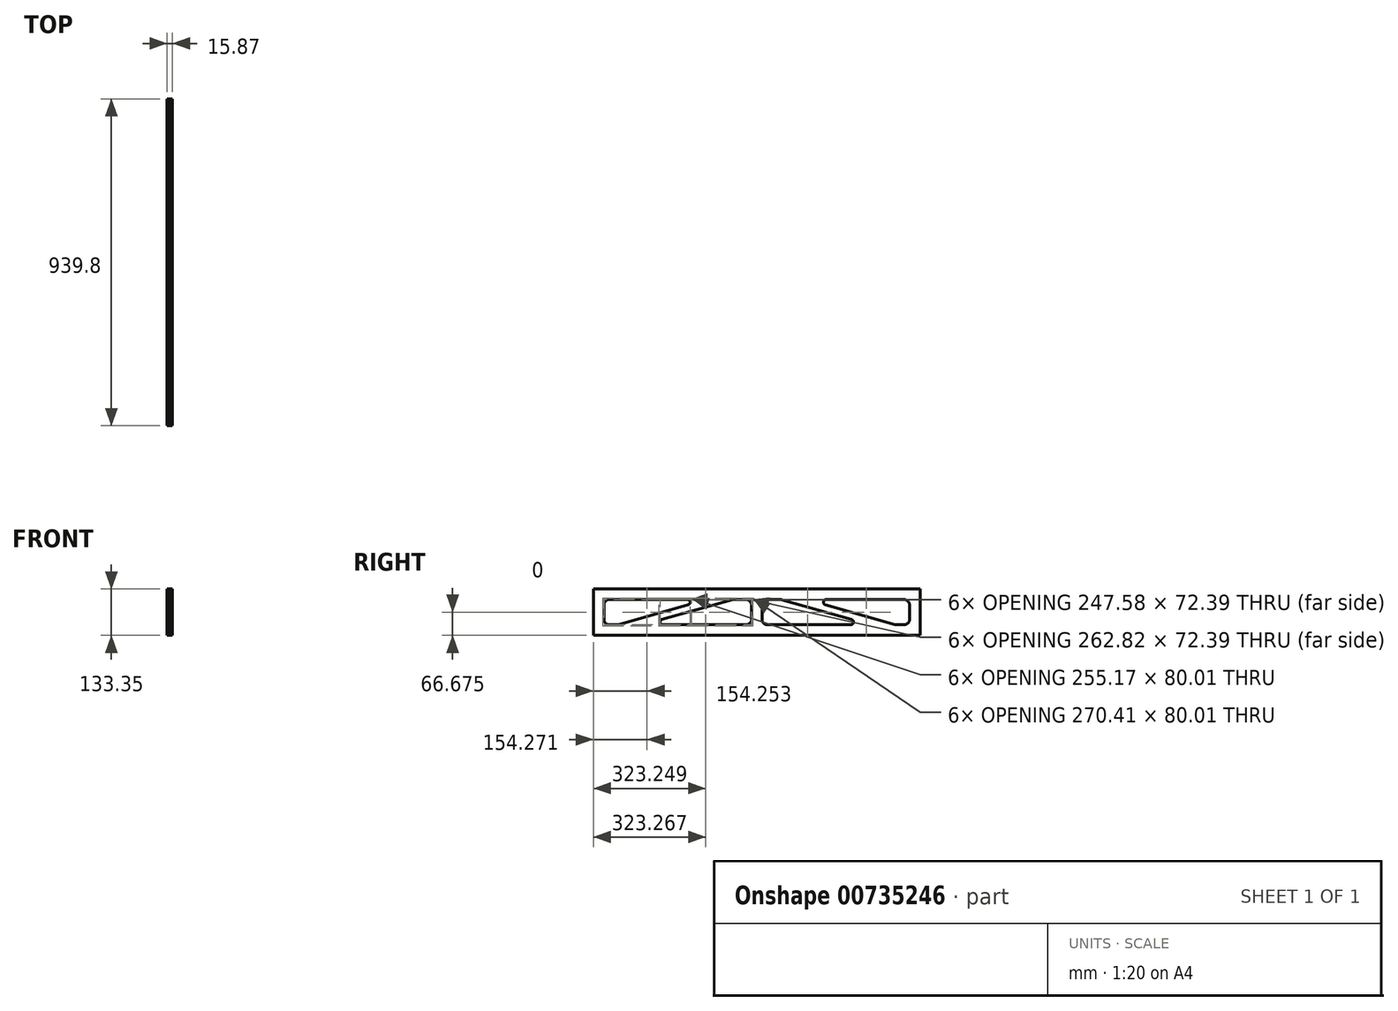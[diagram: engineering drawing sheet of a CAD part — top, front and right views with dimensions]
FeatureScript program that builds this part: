
annotation { "Feature Type Name" : "Feature", "Feature Type Description" : "" }
export const myFeature = defineFeature(function(context is Context, id is Id, definition is map)
    precondition{}
    {
        {
            var Q0;
            Q0=qCreatedBy(makeId("Front.planeOp"),FACE);
            var sketch = newSketch(context, id + "F0", { "sketchPlane" : qUnion([Q0])});
            skLineSegment(sketch, "E0.bottom", {"start": v(247.65, 0) * mm, "end": v(-247.65, 0) * mm});
            skLineSegment(sketch, "E0.top", {"start": v(247.65, 133.35) * mm, "end": v(-247.65, 133.35) * mm});
            skLineSegment(sketch, "E0.left", {"start": v(247.65, 0) * mm, "end": v(247.65, 133.35) * mm});
            skLineSegment(sketch, "E0.right", {"start": v(-247.65, 0) * mm, "end": v(-247.65, 133.35) * mm});
            skPoint(sketch, "E0.middle", {"position": v(0, 66.68) * mm});
            skSolve(sketch);
        }
        {
            var Q0;
            Q0=makeQuery(id+"F0.imprint","IMPRINT",FACE,{"disambiguationData":[TD([[makeQuery(id+"F0.imprint","IMPRINT",EDGE,{"derivedFrom":sQuery(id+"F0.wireOp",EDGE,"E0.bottom")}),-1.0]])]});
            var Q1;
            Q1 = qConstructionFilter(qBodyType(qCreatedBy(id + "F0" ,EDGE), BodyType.WIRE), ConstructionObject.NO);
            extrude(context, id + "F1", {"entities" : qUnion([Q0]), "bodyType" : ToolBodyType.SURFACE, "surfaceEntities" : qUnion([Q1]), "oppositeDirection" : true, "depth" : 939.8 * mm, "offsetDistance" : 25.4 * mm});
        }
        {
            var Q0;
            Q0=makeQuery(id+"F1.opExtrude","SWEPT_FACE",FACE,{"disambiguationData":[OSD([sQuery(id+"F0.wireOp",EDGE,"E0.left")])]});
            var sketch = newSketch(context, id + "F2", { "sketchPlane" : qUnion([Q0])});
            skLineSegment(sketch, "E1.0", {"start": v(0, 0) * mm, "end": v(0, 133.35) * mm});
            skLineSegment(sketch, "E2.0", {"start": v(0, 133.35) * mm, "end": v(-939.8, 133.35) * mm});
            skLineSegment(sketch, "E3.0", {"start": v(0, 0) * mm, "end": v(-939.8, 0) * mm});
            skLineSegment(sketch, "E4.0", {"start": v(-939.8, 133.35) * mm, "end": v(-939.8, 0) * mm});
            skLineSegment(sketch, "E5.0", {"start": v(-30.48, 30.48) * mm, "end": v(-30.48, 102.87) * mm});
            skLineSegment(sketch, "E5.1", {"start": v(-30.48, 30.48) * mm, "end": v(-70.2, 30.48) * mm});
            skLineSegment(sketch, "E5.2", {"start": v(-909.32, 102.87) * mm, "end": v(-909.32, 30.48) * mm});
            skLineSegment(sketch, "E5.3", {"start": v(-30.48, 102.87) * mm, "end": v(-325.28, 102.87) * mm});
            skPoint(sketch, "E6", {"position": v(-469.9, 0) * mm});
            skLineSegment(sketch, "E7", {"start": v(-469.9, 0) * mm, "end": v(-469.9, 133.35) * mm, "construction": true});
            skLineSegment(sketch, "E8", {"start": v(0, 0) * mm, "end": v(-469.9, 133.35) * mm, "construction": true});
            skLineSegment(sketch, "E9", {"start": v(-939.8, 0) * mm, "end": v(-469.9, 133.35) * mm, "construction": true});
            skLineSegment(sketch, "E10", {"start": v(-325.28, 102.87) * mm, "end": v(-70.2, 30.48) * mm});
            skLineSegment(sketch, "E11", {"start": v(-144.62, 30.48) * mm, "end": v(-399.7, 102.87) * mm});
            skLineSegment(sketch, "E12", {"start": v(-454.66, 102.87) * mm, "end": v(-454.66, 30.48) * mm});
            skLineSegment(sketch, "E13", {"start": v(-485.14, 102.87) * mm, "end": v(-485.14, 30.48) * mm});
            skLineSegment(sketch, "E14", {"start": v(-540.1, 102.87) * mm, "end": v(-795.18, 30.48) * mm});
            skLineSegment(sketch, "E15", {"start": v(-614.52, 102.87) * mm, "end": v(-869.6, 30.48) * mm});
            skLineSegment(sketch, "E16.trimOffspring", {"start": v(-399.7, 102.87) * mm, "end": v(-454.66, 102.87) * mm});
            skLineSegment(sketch, "E17.trimOffspring", {"start": v(-144.62, 30.48) * mm, "end": v(-454.66, 30.48) * mm});
            skLineSegment(sketch, "E18.trimOffspring", {"start": v(-485.14, 102.87) * mm, "end": v(-540.1, 102.87) * mm});
            skLineSegment(sketch, "E19.trimOffspring", {"start": v(-485.14, 30.48) * mm, "end": v(-795.18, 30.48) * mm});
            skLineSegment(sketch, "E20.trimOffspring", {"start": v(-614.52, 102.87) * mm, "end": v(-909.32, 102.87) * mm});
            skLineSegment(sketch, "E21.trimOffspring", {"start": v(-869.6, 30.48) * mm, "end": v(-909.32, 30.48) * mm});
            skSolve(sketch);
        }
        {
            var Q0;
            Q0 = qSketchRegion(id + "F2", true);
            extrude(context, id + "F3", {"entities" : qUnion([Q0]), "depth" : 9.52 * mm, "offsetDistance" : 25.4 * mm});
        }
        {
            var Q0;
            Q0=makeQuery(id+"F3.opExtrude","SWEPT_EDGE",EDGE,{"disambiguationData":[OSD([sQuery(id+"F2.wireOp",EDGE,"E11"),sQuery(id+"F2.wireOp",EDGE,"E16.trimOffspring")])]});
            var Q1;
            Q1=makeQuery(id+"F3.opExtrude","SWEPT_EDGE",EDGE,{"disambiguationData":[OSD([sQuery(id+"F2.wireOp",EDGE,"E12"),sQuery(id+"F2.wireOp",EDGE,"E16.trimOffspring")])]});
            var Q2;
            Q2=makeQuery(id+"F3.opExtrude","SWEPT_EDGE",EDGE,{"disambiguationData":[OSD([sQuery(id+"F2.wireOp",EDGE,"E12"),sQuery(id+"F2.wireOp",EDGE,"E17.trimOffspring")])]});
            var Q3;
            Q3=makeQuery(id+"F3.opExtrude","SWEPT_EDGE",EDGE,{"disambiguationData":[OSD([sQuery(id+"F2.wireOp",EDGE,"E5.0"),sQuery(id+"F2.wireOp",EDGE,"E5.1")])]});
            var Q4;
            Q4=makeQuery(id+"F3.opExtrude","SWEPT_EDGE",EDGE,{"disambiguationData":[OSD([sQuery(id+"F2.wireOp",EDGE,"E5.0"),sQuery(id+"F2.wireOp",EDGE,"E5.3")])]});
            var Q5;
            Q5=makeQuery(id+"F3.opExtrude","SWEPT_EDGE",EDGE,{"disambiguationData":[OSD([sQuery(id+"F2.wireOp",EDGE,"E5.1"),sQuery(id+"F2.wireOp",EDGE,"E10")])]});
            var Q6;
            Q6=makeQuery(id+"F3.opExtrude","SWEPT_EDGE",EDGE,{"disambiguationData":[OSD([sQuery(id+"F2.wireOp",EDGE,"E14"),sQuery(id+"F2.wireOp",EDGE,"E18.trimOffspring")])]});
            var Q7;
            Q7=makeQuery(id+"F3.opExtrude","SWEPT_EDGE",EDGE,{"disambiguationData":[OSD([sQuery(id+"F2.wireOp",EDGE,"E13"),sQuery(id+"F2.wireOp",EDGE,"E18.trimOffspring")])]});
            var Q8;
            Q8=makeQuery(id+"F3.opExtrude","SWEPT_EDGE",EDGE,{"disambiguationData":[OSD([sQuery(id+"F2.wireOp",EDGE,"E13"),sQuery(id+"F2.wireOp",EDGE,"E19.trimOffspring")])]});
            var Q9;
            Q9=makeQuery(id+"F3.opExtrude","SWEPT_EDGE",EDGE,{"disambiguationData":[OSD([sQuery(id+"F2.wireOp",EDGE,"E5.2"),sQuery(id+"F2.wireOp",EDGE,"E20.trimOffspring")])]});
            var Q10;
            Q10=makeQuery(id+"F3.opExtrude","SWEPT_EDGE",EDGE,{"disambiguationData":[OSD([sQuery(id+"F2.wireOp",EDGE,"E5.2"),sQuery(id+"F2.wireOp",EDGE,"E21.trimOffspring")])]});
            var Q11;
            Q11=makeQuery(id+"F3.opExtrude","SWEPT_EDGE",EDGE,{"disambiguationData":[OSD([sQuery(id+"F2.wireOp",EDGE,"E15"),sQuery(id+"F2.wireOp",EDGE,"E21.trimOffspring")])]});
            fillet(context, id + "F4", {"entities" : qUnion([Q0, Q1, Q2, Q3, Q4, Q5, Q6, Q7, Q8, Q9, Q10, Q11]), "radius" : 15.24 * mm, "tangentPropagation" : true, "allowEdgeOverflow" : false});
        }
        {
            var Q0;
            Q0=makeQuery(id+"F3.opExtrude","SWEPT_EDGE",EDGE,{"disambiguationData":[OSD([sQuery(id+"F2.wireOp",EDGE,"E11"),sQuery(id+"F2.wireOp",EDGE,"E17.trimOffspring")])]});
            var Q1;
            Q1=makeQuery(id+"F3.opExtrude","SWEPT_EDGE",EDGE,{"disambiguationData":[OSD([sQuery(id+"F2.wireOp",EDGE,"E15"),sQuery(id+"F2.wireOp",EDGE,"E20.trimOffspring")])]});
            var Q2;
            Q2=makeQuery(id+"F3.opExtrude","SWEPT_EDGE",EDGE,{"disambiguationData":[OSD([sQuery(id+"F2.wireOp",EDGE,"E14"),sQuery(id+"F2.wireOp",EDGE,"E19.trimOffspring")])]});
            var Q3;
            Q3=makeQuery(id+"F3.opExtrude","SWEPT_EDGE",EDGE,{"disambiguationData":[OSD([sQuery(id+"F2.wireOp",EDGE,"E5.3"),sQuery(id+"F2.wireOp",EDGE,"E10")])]});
            fillet(context, id + "F5", {"entities" : qUnion([Q0, Q1, Q2, Q3]), "radius" : 7.62 * mm, "tangentPropagation" : true, "allowEdgeOverflow" : false});
        }
        {
            var Q0;
            Q0=makeQuery(id+"F3.opExtrude","CAP_EDGE",EDGE,{"disambiguationData":[OSD([sQuery(id+"F2.wireOp",EDGE,"E5.3")])],"isStart":true});
            var Q1;
            Q1=makeQuery(id+"F3.opExtrude","CAP_EDGE",EDGE,{"disambiguationData":[OSD([sQuery(id+"F2.wireOp",EDGE,"E11")])],"isStart":true});
            var Q2;
            Q2=makeQuery(id+"F3.opExtrude","CAP_EDGE",EDGE,{"disambiguationData":[OSD([sQuery(id+"F2.wireOp",EDGE,"E18.trimOffspring")])],"isStart":true});
            var Q3;
            Q3=makeQuery(id+"F3.opExtrude","CAP_EDGE",EDGE,{"disambiguationData":[OSD([sQuery(id+"F2.wireOp",EDGE,"E20.trimOffspring")])],"isStart":true});
            fillet(context, id + "F6", {"entities" : qUnion([Q0, Q1, Q2, Q3]), "radius" : 3.8 * mm, "tangentPropagation" : true, "allowEdgeOverflow" : false});
        }
        {
            var Q0;
            Q0=makeQuery(id+"F3.opExtrude","CAP_FACE",FACE,{"disambiguationData":[OSD([sQuery(id+"F2.wireOp",EDGE,"E1.0"),sQuery(id+"F2.wireOp",EDGE,"E2.0"),sQuery(id+"F2.wireOp",EDGE,"E3.0"),sQuery(id+"F2.wireOp",EDGE,"E4.0"),sQuery(id+"F2.wireOp",EDGE,"E5.0"),sQuery(id+"F2.wireOp",EDGE,"E5.1"),sQuery(id+"F2.wireOp",EDGE,"E5.2"),sQuery(id+"F2.wireOp",EDGE,"E5.3"),sQuery(id+"F2.wireOp",EDGE,"E10"),sQuery(id+"F2.wireOp",EDGE,"E11"),sQuery(id+"F2.wireOp",EDGE,"E12"),sQuery(id+"F2.wireOp",EDGE,"E13"),sQuery(id+"F2.wireOp",EDGE,"E14"),sQuery(id+"F2.wireOp",EDGE,"E15"),sQuery(id+"F2.wireOp",EDGE,"E16.trimOffspring"),sQuery(id+"F2.wireOp",EDGE,"E17.trimOffspring"),sQuery(id+"F2.wireOp",EDGE,"E18.trimOffspring"),sQuery(id+"F2.wireOp",EDGE,"E19.trimOffspring"),sQuery(id+"F2.wireOp",EDGE,"E20.trimOffspring"),sQuery(id+"F2.wireOp",EDGE,"E21.trimOffspring")])],"isStart":false});
            var sketch = newSketch(context, id + "F7", { "sketchPlane" : qUnion([Q0])});
            skLineSegment(sketch, "E22.0", {"start": v(0, 133.35) * mm, "end": v(-939.8, 133.35) * mm});
            skLineSegment(sketch, "E23.0", {"start": v(-939.8, 0) * mm, "end": v(-939.8, 133.35) * mm});
            skLineSegment(sketch, "E24.0", {"start": v(0, 0) * mm, "end": v(-939.8, 0) * mm});
            skLineSegment(sketch, "E25.0", {"start": v(0, 0) * mm, "end": v(0, 133.35) * mm});
            skSolve(sketch);
        }
        {
            var Q0;
            Q0 = qSketchRegion(id + "F7", true);
            extrude(context, id + "F8", {"entities" : qUnion([Q0]), "depth" : 6.35 * mm, "offsetDistance" : 25.4 * mm});
        }
    });
